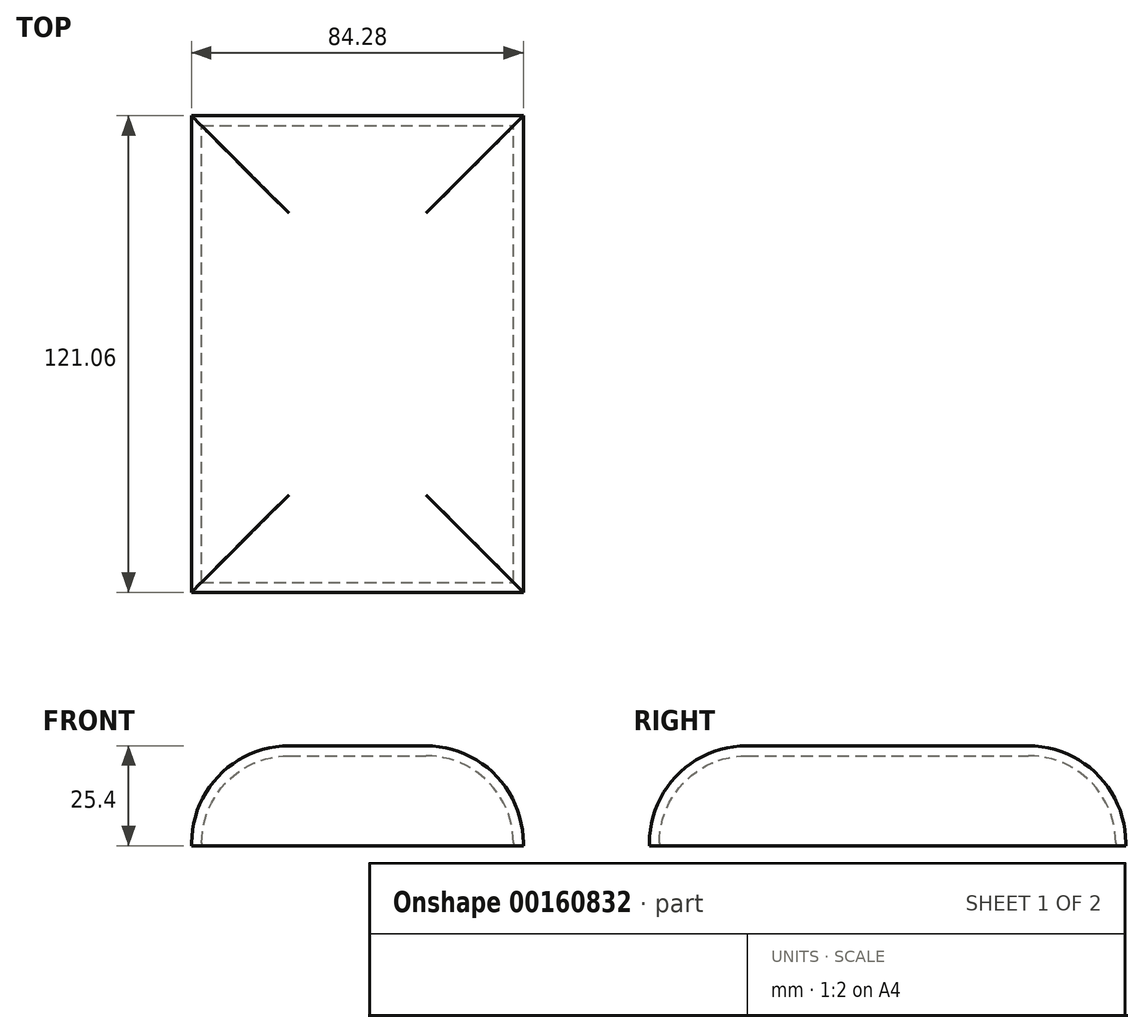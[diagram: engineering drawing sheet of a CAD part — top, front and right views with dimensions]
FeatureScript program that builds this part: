
annotation { "Feature Type Name" : "Feature", "Feature Type Description" : "" }
export const myFeature = defineFeature(function(context is Context, id is Id, definition is map)
    precondition{}
    {
        {
            var Q0;
            Q0=qCreatedBy(makeId("Top.planeOp"),FACE);
            var sketch = newSketch(context, id + "F0", { "sketchPlane" : qUnion([Q0])});
            skLineSegment(sketch, "E0.bottom", {"start": v(0, -23.02) * mm, "end": v(84.28, -23.02) * mm});
            skLineSegment(sketch, "E0.top", {"start": v(0, 98.04) * mm, "end": v(84.28, 98.04) * mm});
            skLineSegment(sketch, "E0.left", {"start": v(0, -23.02) * mm, "end": v(0, 98.04) * mm});
            skLineSegment(sketch, "E0.right", {"start": v(84.28, -23.02) * mm, "end": v(84.28, 98.04) * mm});
            skSolve(sketch);
        }
        {
            var Q0;
            Q0=makeQuery(id+"F0.imprint","IMPRINT",FACE,{"disambiguationData":[TD([[makeQuery(id+"F0.imprint","IMPRINT",EDGE,{"derivedFrom":sQuery(id+"F0.wireOp",EDGE,"E0.bottom")}),1.0]])]});
            extrude(context, id + "F1", {"entities" : qUnion([Q0]), "depth" : 25.4 * mm});
        }
        {
            var Q0;
            Q0=makeQuery(id+"F1.opExtrude","CAP_FACE",FACE,{"disambiguationData":[OSD([sQuery(id+"F0.wireOp",EDGE,"E0.bottom"),sQuery(id+"F0.wireOp",EDGE,"E0.top"),sQuery(id+"F0.wireOp",EDGE,"E0.left"),sQuery(id+"F0.wireOp",EDGE,"E0.right")])],"isStart":false});
            fillet(context, id + "F2", {"entities" : qUnion([Q0]), "radius" : 24.74 * mm, "tangentPropagation" : true, "allowEdgeOverflow" : false});
        }
        {
            var Q0;
            Q0=makeQuery(id+"F1.opExtrude","CAP_FACE",FACE,{"disambiguationData":[OSD([sQuery(id+"F0.wireOp",EDGE,"E0.bottom"),sQuery(id+"F0.wireOp",EDGE,"E0.top"),sQuery(id+"F0.wireOp",EDGE,"E0.left"),sQuery(id+"F0.wireOp",EDGE,"E0.right")])],"isStart":true});
            shell(context, id + "F3", {"entities" : qUnion([Q0]), "thickness" : 2.54 * mm});
        }
    });
